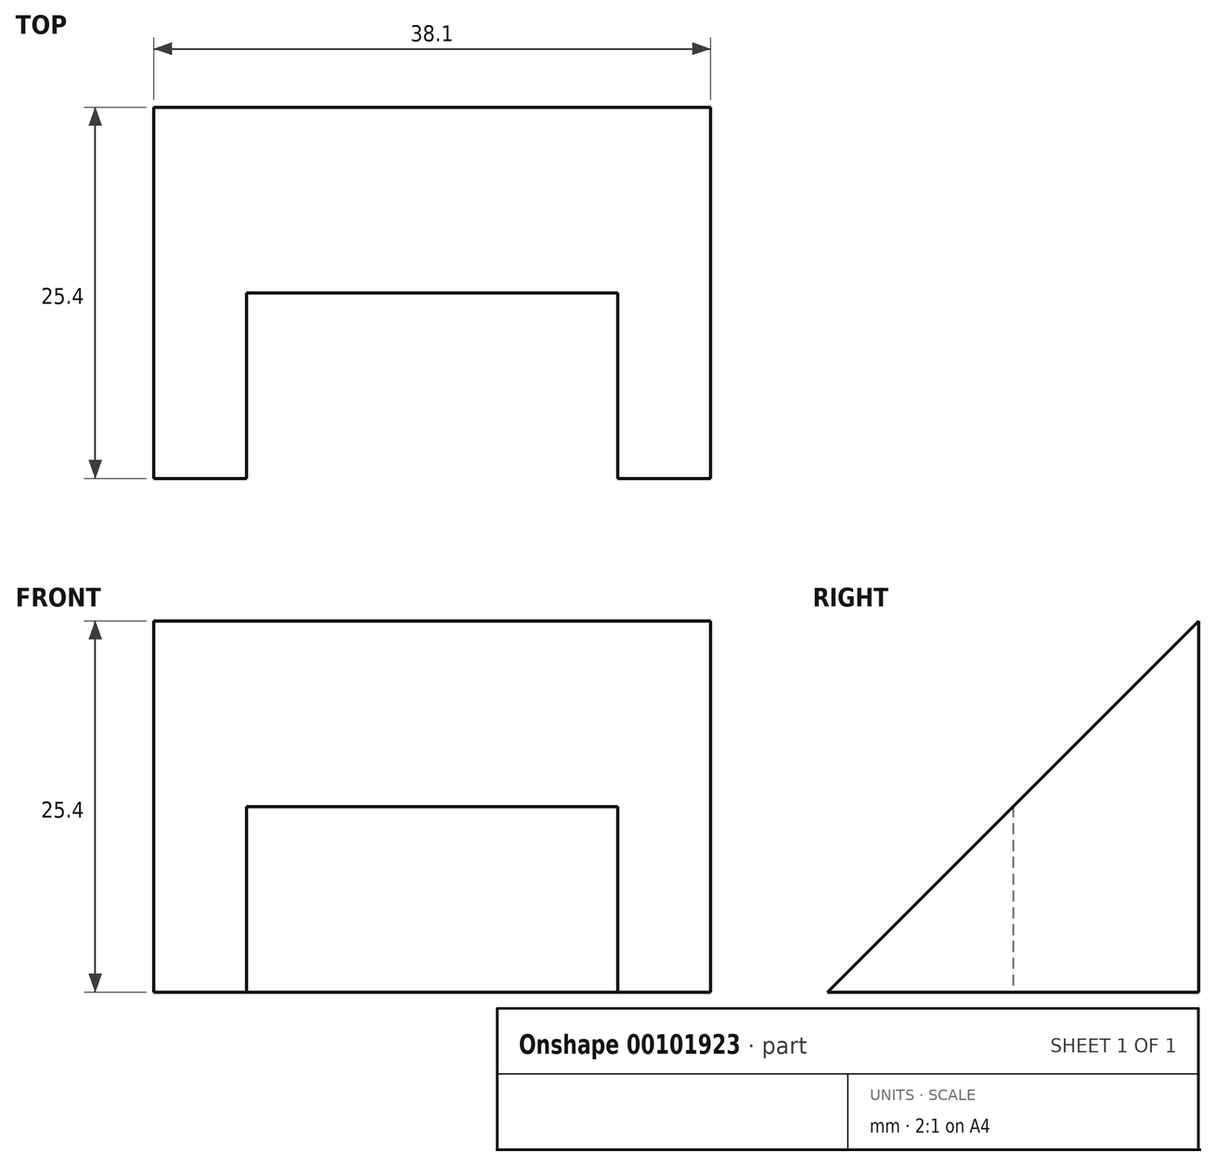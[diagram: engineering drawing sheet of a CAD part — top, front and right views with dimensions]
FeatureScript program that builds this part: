
annotation { "Feature Type Name" : "Feature", "Feature Type Description" : "" }
export const myFeature = defineFeature(function(context is Context, id is Id, definition is map)
    precondition{}
    {
        {
            var Q0;
            Q0=qCreatedBy(makeId("Front.planeOp"),FACE);
            var sketch = newSketch(context, id + "F0", { "sketchPlane" : qUnion([Q0])});
            skLineSegment(sketch, "E0.bottom", {"start": v(-19.05, 0) * mm, "end": v(19.05, 0) * mm});
            skLineSegment(sketch, "E0.top", {"start": v(-19.05, 25.4) * mm, "end": v(19.05, 25.4) * mm});
            skLineSegment(sketch, "E0.left", {"start": v(-19.05, 0) * mm, "end": v(-19.05, 25.4) * mm});
            skLineSegment(sketch, "E0.right", {"start": v(19.05, 0) * mm, "end": v(19.05, 25.4) * mm});
            skSolve(sketch);
        }
        {
            var Q0;
            Q0 = qSketchRegion(id + "F0", true);
            extrude(context, id + "F1", {"entities" : qUnion([Q0]), "depth" : 25.4 * mm});
        }
        {
            var Q0;
            Q0=qCreatedBy(makeId("Right.planeOp"),FACE);
            var sketch = newSketch(context, id + "F2", { "sketchPlane" : qUnion([Q0])});
            skLineSegment(sketch, "E1", {"start": v(0, 25.4) * mm, "end": v(-25.4, 0) * mm});
            skLineSegment(sketch, "E2", {"start": v(-25.4, 0) * mm, "end": v(-25.4, 25.4) * mm});
            skLineSegment(sketch, "E3", {"start": v(-25.4, 25.4) * mm, "end": v(0, 25.4) * mm});
            skSolve(sketch);
        }
        {
            var Q0;
            Q0 = qSketchRegion(id + "F2", true);
            extrude(context, id + "F3", {"entities" : qUnion([Q0]), "operationType" : NewBodyOperationType.REMOVE, "endBound" : BoundingType.THROUGH_ALL, "depth" : 25.4 * mm, "hasSecondDirection" : true, "secondDirectionOppositeDirection" : true, "secondDirectionDepth" : 25.4 * mm});
        }
        {
            var Q0;
            Q0=qCreatedBy(makeId("Top.planeOp"),FACE);
            var sketch = newSketch(context, id + "F4", { "sketchPlane" : qUnion([Q0])});
            skLineSegment(sketch, "E4.bottom", {"start": v(-12.7, -25.4) * mm, "end": v(12.7, -25.4) * mm});
            skLineSegment(sketch, "E4.left", {"start": v(-12.7, -25.4) * mm, "end": v(-12.7, -12.7) * mm});
            skLineSegment(sketch, "E4.right", {"start": v(12.7, -25.4) * mm, "end": v(12.7, -12.7) * mm});
            skLineSegment(sketch, "E5", {"start": v(-12.7, -12.7) * mm, "end": v(12.7, -12.7) * mm});
            skSolve(sketch);
        }
        {
            var Q0;
            Q0 = qSketchRegion(id + "F4", true);
            extrude(context, id + "F5", {"entities" : qUnion([Q0]), "operationType" : NewBodyOperationType.REMOVE, "endBound" : BoundingType.THROUGH_ALL, "depth" : 25.4 * mm});
        }
    });
